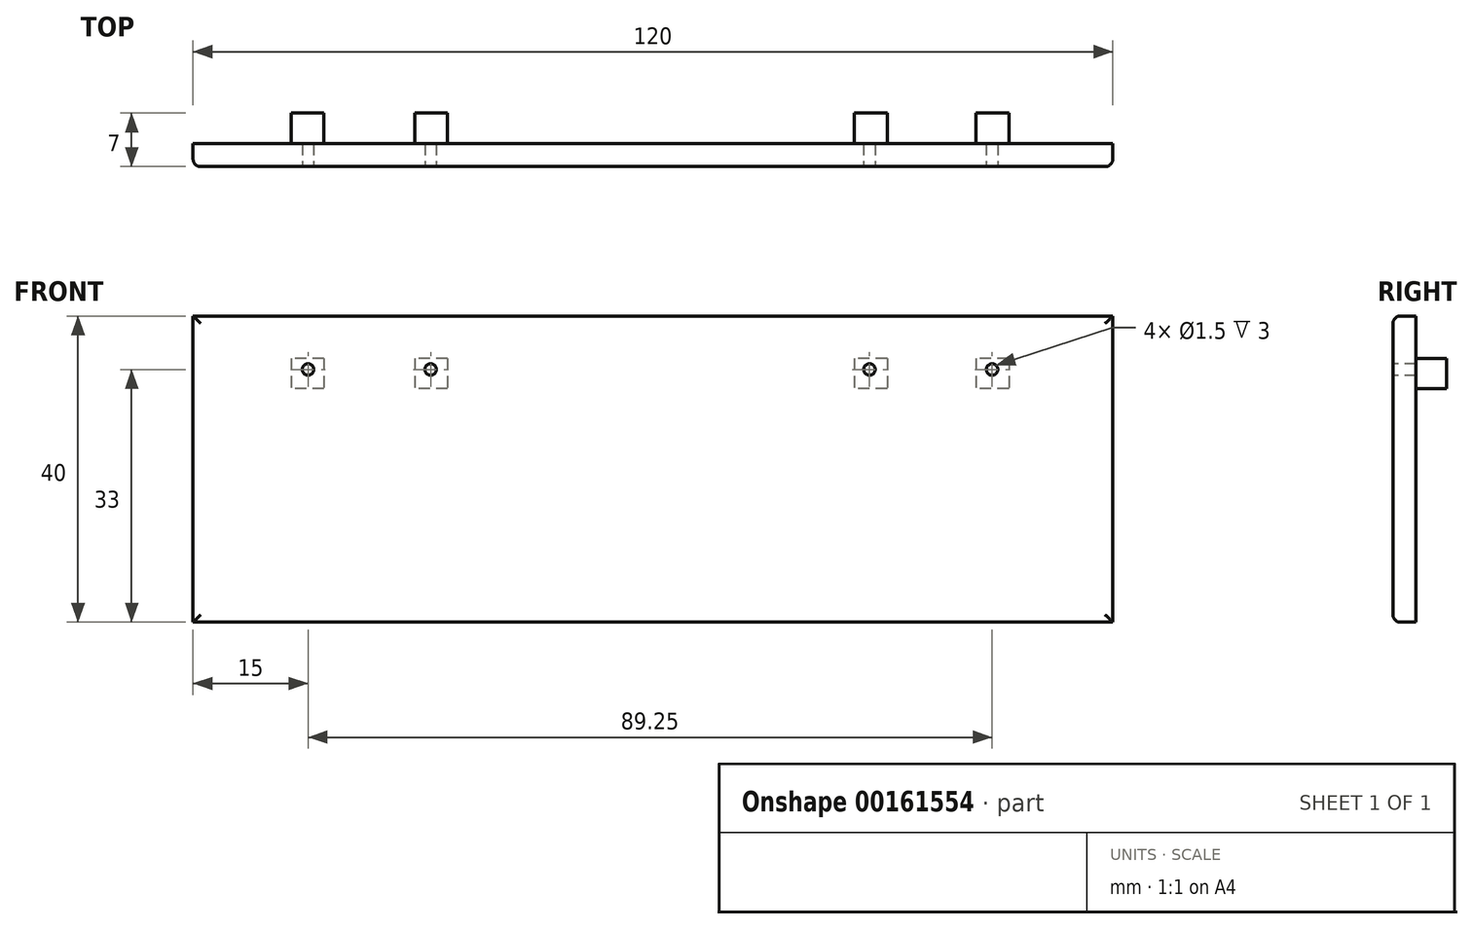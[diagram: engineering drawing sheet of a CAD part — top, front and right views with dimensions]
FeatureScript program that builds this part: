
annotation { "Feature Type Name" : "Feature", "Feature Type Description" : "" }
export const myFeature = defineFeature(function(context is Context, id is Id, definition is map)
    precondition{}
    {
        {
            var Q0;
            Q0=qCreatedBy(makeId("Front.planeOp"),FACE);
            var sketch = newSketch(context, id + "F0", { "sketchPlane" : qUnion([Q0])});
            skLineSegment(sketch, "E0.bottom", {"start": v(-60, 20) * mm, "end": v(60, 20) * mm});
            skLineSegment(sketch, "E0.top", {"start": v(-60, -20) * mm, "end": v(60, -20) * mm});
            skLineSegment(sketch, "E0.left", {"start": v(-60, 20) * mm, "end": v(-60, -20) * mm});
            skLineSegment(sketch, "E0.right", {"start": v(60, 20) * mm, "end": v(60, -20) * mm});
            skPoint(sketch, "E0.middle", {"position": v(0, 0) * mm});
            skSolve(sketch);
        }
        {
            var Q0;
            Q0 = qSketchRegion(id + "F0", true);
            extrude(context, id + "F1", {"entities" : qUnion([Q0]), "depth" : 3 * mm});
        }
        {
            var Q0;
            Q0=makeQuery(id+"F1.opExtrude","CAP_FACE",FACE,{"disambiguationData":[OSD([sQuery(id+"F0.wireOp",EDGE,"E0.bottom"),sQuery(id+"F0.wireOp",EDGE,"E0.top"),sQuery(id+"F0.wireOp",EDGE,"E0.left"),sQuery(id+"F0.wireOp",EDGE,"E0.right")])],"isStart":false});
            fillet(context, id + "F2", {"entities" : qUnion([Q0]), "radius" : 1 * mm, "tangentPropagation" : true, "allowEdgeOverflow" : false});
        }
        {
            var Q0;
            Q0=makeQuery(id+"F1.opExtrude","CAP_FACE",FACE,{"disambiguationData":[OSD([sQuery(id+"F0.wireOp",EDGE,"E0.bottom"),sQuery(id+"F0.wireOp",EDGE,"E0.top"),sQuery(id+"F0.wireOp",EDGE,"E0.left"),sQuery(id+"F0.wireOp",EDGE,"E0.right")])],"isStart":false});
            var sketch = newSketch(context, id + "F3", { "sketchPlane" : qUnion([Q0])});
            skCircle(sketch, "E1", {"center": v(-45, 13) * mm, "radius": 0.75 * mm});
            skCircle(sketch, "E2", {"center": v(-29, 13) * mm, "radius": 0.75 * mm});
            skCircle(sketch, "E3", {"center": v(28.25, 13) * mm, "radius": 0.75 * mm});
            skCircle(sketch, "E4", {"center": v(44.25, 13) * mm, "radius": 0.75 * mm});
            skSolve(sketch);
        }
        {
            var Q0;
            Q0 = qSketchRegion(id + "F3", true);
            extrude(context, id + "F4", {"entities" : qUnion([Q0]), "operationType" : NewBodyOperationType.REMOVE, "oppositeDirection" : true, "depth" : 5.9 * mm});
        }
        {
            var Q0;
            Q0=makeQuery(id+"F1.opExtrude","CAP_FACE",FACE,{"disambiguationData":[OSD([sQuery(id+"F0.wireOp",EDGE,"E0.bottom"),sQuery(id+"F0.wireOp",EDGE,"E0.top"),sQuery(id+"F0.wireOp",EDGE,"E0.left"),sQuery(id+"F0.wireOp",EDGE,"E0.right")])],"isStart":true});
            var sketch = newSketch(context, id + "F5", { "sketchPlane" : qUnion([Q0])});
            skLineSegment(sketch, "E5.bottom", {"start": v(-46.44, 14.44) * mm, "end": v(-42.13, 14.44) * mm});
            skLineSegment(sketch, "E5.top", {"start": v(-46.44, 10.53) * mm, "end": v(-42.13, 10.53) * mm});
            skLineSegment(sketch, "E5.left", {"start": v(-46.44, 14.44) * mm, "end": v(-46.44, 10.53) * mm});
            skLineSegment(sketch, "E5.right", {"start": v(-42.13, 14.44) * mm, "end": v(-42.13, 10.53) * mm});
            skLineSegment(sketch, "E6.bottom", {"start": v(-30.56, 14.44) * mm, "end": v(-26.25, 14.44) * mm});
            skLineSegment(sketch, "E6.top", {"start": v(-30.56, 10.53) * mm, "end": v(-26.25, 10.53) * mm});
            skLineSegment(sketch, "E6.left", {"start": v(-30.56, 14.44) * mm, "end": v(-30.56, 10.53) * mm});
            skLineSegment(sketch, "E6.right", {"start": v(-26.25, 14.44) * mm, "end": v(-26.25, 10.53) * mm});
            skLineSegment(sketch, "E7.bottom", {"start": v(26.8, 14.44) * mm, "end": v(31.1, 14.44) * mm});
            skLineSegment(sketch, "E7.top", {"start": v(26.8, 10.53) * mm, "end": v(31.1, 10.53) * mm});
            skLineSegment(sketch, "E7.left", {"start": v(26.8, 14.44) * mm, "end": v(26.8, 10.53) * mm});
            skLineSegment(sketch, "E7.right", {"start": v(31.1, 14.44) * mm, "end": v(31.1, 10.53) * mm});
            skLineSegment(sketch, "E8.bottom", {"start": v(42.92, 14.44) * mm, "end": v(47.22, 14.44) * mm});
            skLineSegment(sketch, "E8.top", {"start": v(42.92, 10.53) * mm, "end": v(47.22, 10.53) * mm});
            skLineSegment(sketch, "E8.left", {"start": v(42.92, 14.44) * mm, "end": v(42.92, 10.53) * mm});
            skLineSegment(sketch, "E8.right", {"start": v(47.22, 14.44) * mm, "end": v(47.22, 10.53) * mm});
            skSolve(sketch);
        }
        {
            var Q0;
            Q0 = qSketchRegion(id + "F5", true);
            extrude(context, id + "F6", {"entities" : qUnion([Q0]), "operationType" : NewBodyOperationType.ADD, "depth" : 4 * mm});
        }
    });
